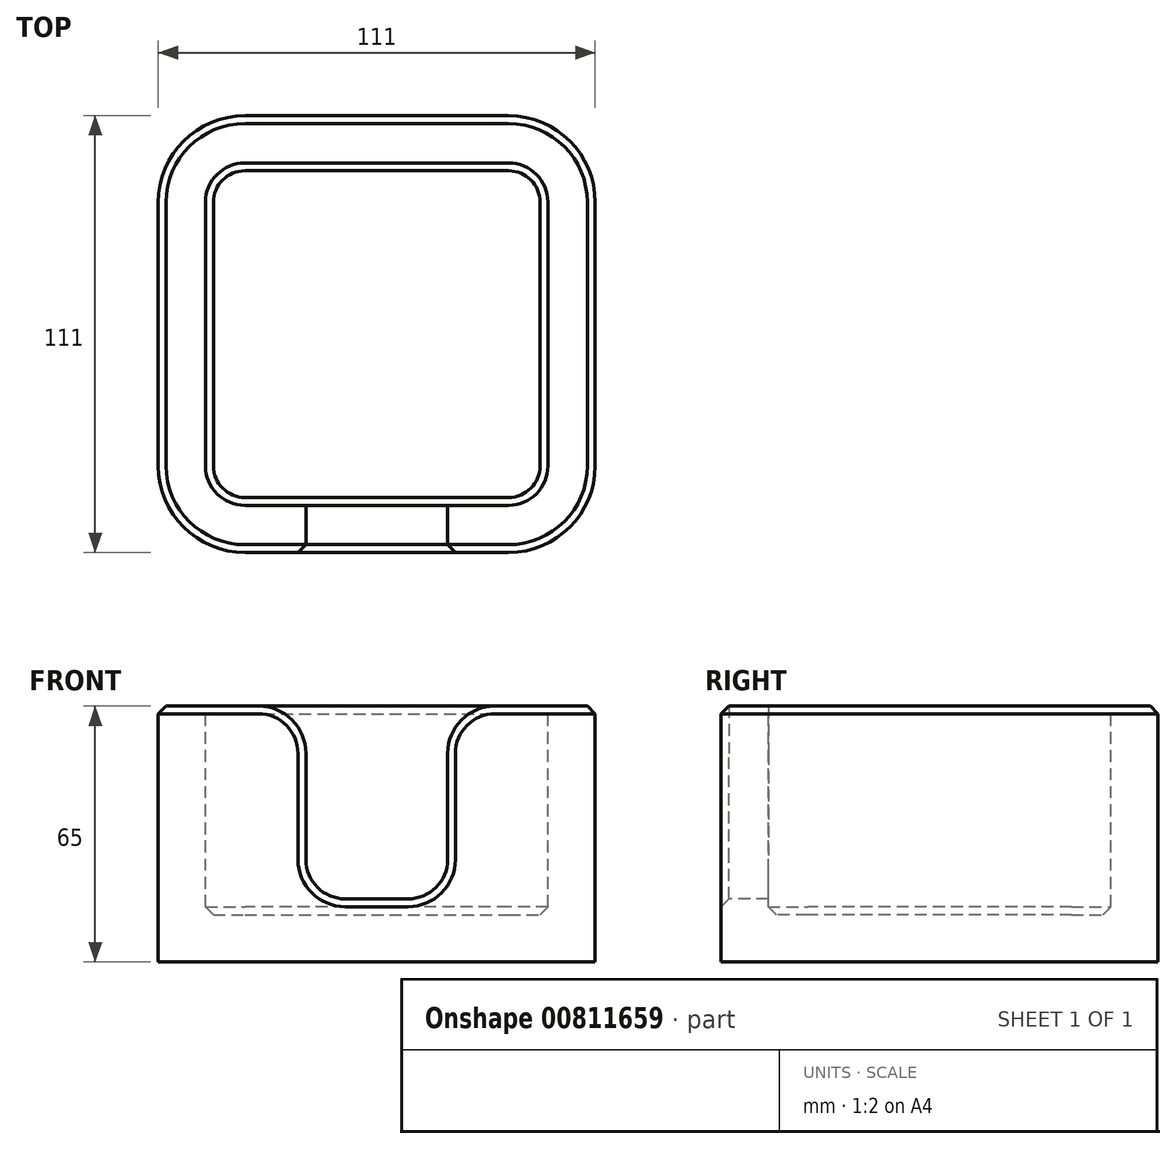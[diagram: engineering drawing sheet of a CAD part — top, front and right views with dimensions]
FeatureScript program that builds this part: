
annotation { "Feature Type Name" : "Feature", "Feature Type Description" : "" }
export const myFeature = defineFeature(function(context is Context, id is Id, definition is map)
    precondition{}
    {
        {
            var Q0;
            Q0=qCreatedBy(makeId("Top.planeOp"),FACE);
            var sketch = newSketch(context, id + "F0", { "sketchPlane" : qUnion([Q0])});
            skLineSegment(sketch, "E0.bottom", {"start": v(38, 38) * mm, "end": v(-38, 38) * mm, "construction": true});
            skLineSegment(sketch, "E0.top", {"start": v(38, -38) * mm, "end": v(-38, -38) * mm, "construction": true});
            skLineSegment(sketch, "E0.left", {"start": v(38, 38) * mm, "end": v(38, -38) * mm, "construction": true});
            skLineSegment(sketch, "E0.right", {"start": v(-38, 38) * mm, "end": v(-38, -38) * mm, "construction": true});
            skPoint(sketch, "E0.middle", {"position": v(0, 0) * mm});
            skLineSegment(sketch, "E1.bottom", {"start": v(33.5, 43.5) * mm, "end": v(-33.5, 43.5) * mm, "construction": true});
            skLineSegment(sketch, "E1.top", {"start": v(33.5, -43.5) * mm, "end": v(-33.5, -43.5) * mm, "construction": true});
            skLineSegment(sketch, "E1.left", {"start": v(43.5, 33.5) * mm, "end": v(43.5, -33.5) * mm, "construction": true});
            skLineSegment(sketch, "E1.right", {"start": v(-43.5, 33.5) * mm, "end": v(-43.5, -33.5) * mm, "construction": true});
            skPoint(sketch, "E2.visualSharp", {"position": v(-43.5, 43.5) * mm});
            skArc(sketch, "E2.filletArc", {"start": v(-33.5, 43.5) * mm, "mid": v(-40.57, 40.57) * mm, "end": v(-43.5, 33.5) * mm, "construction": true});
            skPoint(sketch, "E3.visualSharp", {"position": v(43.5, 43.5) * mm});
            skArc(sketch, "E3.filletArc", {"start": v(43.5, 33.5) * mm, "mid": v(40.57, 40.57) * mm, "end": v(33.5, 43.5) * mm, "construction": true});
            skPoint(sketch, "E4.visualSharp", {"position": v(43.5, -43.5) * mm});
            skArc(sketch, "E4.filletArc", {"start": v(33.5, -43.5) * mm, "mid": v(40.57, -40.57) * mm, "end": v(43.5, -33.5) * mm, "construction": true});
            skPoint(sketch, "E5.visualSharp", {"position": v(-43.5, -43.5) * mm});
            skArc(sketch, "E5.filletArc", {"start": v(-43.5, -33.5) * mm, "mid": v(-40.57, -40.57) * mm, "end": v(-33.5, -43.5) * mm, "construction": true});
            skArc(sketch, "E6.0", {"start": v(55.5, 33.5) * mm, "mid": v(49.06, 49.06) * mm, "end": v(33.5, 55.5) * mm});
            skLineSegment(sketch, "E6.1", {"start": v(33.5, 55.5) * mm, "end": v(-33.5, 55.5) * mm});
            skLineSegment(sketch, "E6.2", {"start": v(55.5, 33.5) * mm, "end": v(55.5, -33.5) * mm});
            skArc(sketch, "E6.3", {"start": v(-33.5, 55.5) * mm, "mid": v(-49.06, 49.06) * mm, "end": v(-55.5, 33.5) * mm});
            skArc(sketch, "E6.4", {"start": v(33.5, -55.5) * mm, "mid": v(49.06, -49.06) * mm, "end": v(55.5, -33.5) * mm});
            skLineSegment(sketch, "E6.5", {"start": v(33.5, -55.5) * mm, "end": v(-33.5, -55.5) * mm});
            skArc(sketch, "E6.6", {"start": v(-55.5, -33.5) * mm, "mid": v(-49.06, -49.06) * mm, "end": v(-33.5, -55.5) * mm});
            skLineSegment(sketch, "E6.7", {"start": v(-55.5, 33.5) * mm, "end": v(-55.5, -33.5) * mm});
            skSolve(sketch);
        }
        {
            var Q0;
            Q0=makeQuery(id+"F0.imprint","IMPRINT",FACE,{"disambiguationData":[TD([[makeQuery(id+"F0.imprint","IMPRINT",EDGE,{"derivedFrom":sQuery(id+"F0.wireOp",EDGE,"E6.0")}),1.0]])]});
            extrude(context, id + "F1", {"entities" : qUnion([Q0]), "depth" : 65 * mm, "offsetDistance" : 25 * mm});
        }
        {
            var Q0;
            Q0=makeQuery(id+"F1.opExtrude","CAP_FACE",FACE,{"disambiguationData":[OSD([sQuery(id+"F0.wireOp",EDGE,"E6.0"),sQuery(id+"F0.wireOp",EDGE,"E6.1"),sQuery(id+"F0.wireOp",EDGE,"E6.2"),sQuery(id+"F0.wireOp",EDGE,"E6.3"),sQuery(id+"F0.wireOp",EDGE,"E6.4"),sQuery(id+"F0.wireOp",EDGE,"E6.5"),sQuery(id+"F0.wireOp",EDGE,"E6.6"),sQuery(id+"F0.wireOp",EDGE,"E6.7")])],"isStart":false});
            var sketch = newSketch(context, id + "F2", { "sketchPlane" : qUnion([Q0])});
            skArc(sketch, "E7.0", {"start": v(-33.5, 43.5) * mm, "mid": v(-40.57, 40.57) * mm, "end": v(-43.5, 33.5) * mm});
            skLineSegment(sketch, "E7.1", {"start": v(33.5, 43.5) * mm, "end": v(-33.5, 43.5) * mm});
            skLineSegment(sketch, "E7.2", {"start": v(-43.5, 33.5) * mm, "end": v(-43.5, -33.5) * mm});
            skArc(sketch, "E7.3", {"start": v(43.5, 33.5) * mm, "mid": v(40.57, 40.57) * mm, "end": v(33.5, 43.5) * mm});
            skArc(sketch, "E7.4", {"start": v(-43.5, -33.5) * mm, "mid": v(-40.57, -40.57) * mm, "end": v(-33.5, -43.5) * mm});
            skLineSegment(sketch, "E7.5", {"start": v(33.5, -43.5) * mm, "end": v(-33.5, -43.5) * mm});
            skArc(sketch, "E7.6", {"start": v(33.5, -43.5) * mm, "mid": v(40.57, -40.57) * mm, "end": v(43.5, -33.5) * mm});
            skLineSegment(sketch, "E7.7", {"start": v(43.5, 33.5) * mm, "end": v(43.5, -33.5) * mm});
            skSolve(sketch);
        }
        {
            var Q0;
            Q0=makeQuery(id+"F2.imprint","IMPRINT",FACE,{"disambiguationData":[TD([[makeQuery(id+"F2.imprint","IMPRINT",EDGE,{"derivedFrom":sQuery(id+"F2.wireOp",EDGE,"E7.0")}),1.0]])]});
            var Q1;
            Q1=makeQuery(id+"F1.opExtrude","CAP_FACE",FACE,{"disambiguationData":[OSD([sQuery(id+"F0.wireOp",EDGE,"E6.0"),sQuery(id+"F0.wireOp",EDGE,"E6.1"),sQuery(id+"F0.wireOp",EDGE,"E6.2"),sQuery(id+"F0.wireOp",EDGE,"E6.3"),sQuery(id+"F0.wireOp",EDGE,"E6.4"),sQuery(id+"F0.wireOp",EDGE,"E6.5"),sQuery(id+"F0.wireOp",EDGE,"E6.6"),sQuery(id+"F0.wireOp",EDGE,"E6.7")])],"isStart":true});
            extrude(context, id + "F3", {"entities" : qUnion([Q0]), "operationType" : NewBodyOperationType.REMOVE, "endBound" : BoundingType.UP_TO_SURFACE, "oppositeDirection" : true, "depth" : 25 * mm, "endBoundEntityFace" : qUnion([Q1]), "hasOffset" : true, "offsetDistance" : 12 * mm});
        }
        {
            var Q0;
            Q0=makeQuery(id+"F1.opExtrude","SWEPT_FACE",FACE,{"disambiguationData":[OSD([sQuery(id+"F0.wireOp",EDGE,"E6.5")])]});
            var sketch = newSketch(context, id + "F4", { "sketchPlane" : qUnion([Q0])});
            skArc(sketch, "E8", {"start": v(-18, 53) * mm, "mid": v(-21.51, 61.49) * mm, "end": v(-30, 65) * mm});
            skArc(sketch, "E9", {"start": v(30, 65) * mm, "mid": v(21.51, 61.49) * mm, "end": v(18, 53) * mm});
            skLineSegment(sketch, "E10", {"start": v(-30, 65) * mm, "end": v(30, 65) * mm});
            skPoint(sketch, "E11", {"position": v(0, 65) * mm});
            skLineSegment(sketch, "E12", {"start": v(-18, 53) * mm, "end": v(-18, 26) * mm});
            skLineSegment(sketch, "E13", {"start": v(-8, 16) * mm, "end": v(8, 16) * mm});
            skLineSegment(sketch, "E14", {"start": v(18, 26) * mm, "end": v(18, 53) * mm});
            skPoint(sketch, "E15.visualSharp", {"position": v(-18, 16) * mm});
            skArc(sketch, "E15.filletArc", {"start": v(-18, 26) * mm, "mid": v(-15.07, 18.93) * mm, "end": v(-8, 16) * mm});
            skPoint(sketch, "E16.visualSharp", {"position": v(18, 16) * mm});
            skArc(sketch, "E16.filletArc", {"start": v(8, 16) * mm, "mid": v(15.07, 18.93) * mm, "end": v(18, 26) * mm});
            skSolve(sketch);
        }
        {
            var Q0;
            Q0=makeQuery(id+"F4.imprint","IMPRINT",FACE,{"disambiguationData":[TD([[makeQuery(id+"F4.imprint","IMPRINT",EDGE,{"derivedFrom":sQuery(id+"F4.wireOp",EDGE,"E8")}),-1.0]])]});
            extrude(context, id + "F5", {"entities" : qUnion([Q0]), "operationType" : NewBodyOperationType.REMOVE, "endBound" : BoundingType.UP_TO_NEXT, "oppositeDirection" : true, "depth" : 25 * mm, "offsetDistance" : 25 * mm});
        }
        {
            var Q0;
            Q0=makeQuery(id+"F1.opExtrude","CAP_EDGE",EDGE,{"disambiguationData":[OSD([sQuery(id+"F0.wireOp",EDGE,"E6.2")])],"isStart":false});
            var Q1;
            Q1=makeQuery(id+"F3.boolean.opBoolean","COPY",EDGE,{"derivedFrom":makeQuery(id+"F3.opExtrude","CAP_EDGE",EDGE,{"disambiguationData":[OSD([sQuery(id+"F2.wireOp",EDGE,"E7.2")])],"isStart":true})});
            var Q2;
            Q2=makeQuery(id+"F3.boolean.opBoolean","COPY",FACE,{"derivedFrom":makeQuery(id+"F3.opExtrude","CAP_FACE",FACE,{"disambiguationData":[OSD([sQuery(id+"F2.wireOp",EDGE,"E7.0"),sQuery(id+"F2.wireOp",EDGE,"E7.1"),sQuery(id+"F2.wireOp",EDGE,"E7.2"),sQuery(id+"F2.wireOp",EDGE,"E7.3"),sQuery(id+"F2.wireOp",EDGE,"E7.4"),sQuery(id+"F2.wireOp",EDGE,"E7.5"),sQuery(id+"F2.wireOp",EDGE,"E7.6"),sQuery(id+"F2.wireOp",EDGE,"E7.7")])],"isStart":false})});
            chamfer(context, id + "F6", {"entities" : qUnion([Q0, Q1, Q2]), "width" : 2 * mm, "tangentPropagation" : true});
        }
    });
